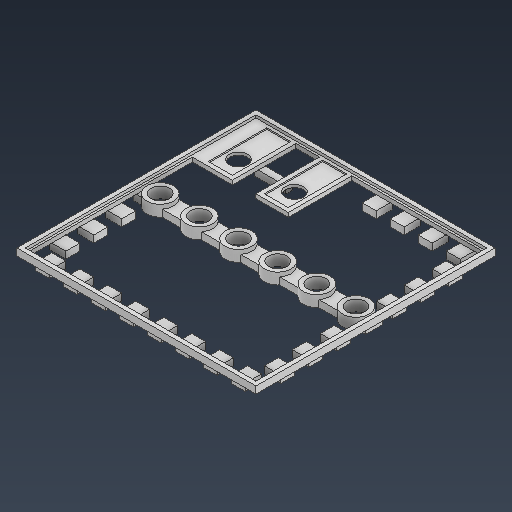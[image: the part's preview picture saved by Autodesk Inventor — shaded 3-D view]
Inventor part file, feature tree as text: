
AUTODESK INVENTOR PART (.ipt)
format: ipt  version: 2025.3 (Build 293356000, 356)  size: 868,864 bytes
history: native  units: mm
features: projected_geometry x26, sketch x20, extrude x8, fillet x1
ambient origin geometry x8: Origin, YZ Plane, XZ Plane, XY Plane, X Axis, Y Axis, Z Axis, Center Point
bodies: Solid1 (feature_tree)
feature tree (55):
  extrude  "Extrusion1"  Depth=171.0mm
  extrude  "Extrusion3"  Depth=60.0mm
  extrude  "Extrusion5"  Depth=78.0mm
  extrude  "Extrusion6"  Depth=75.0mm
  extrude  "Extrusion7"  Depth=30.0mm
  extrude  "Extrusion8"  Depth=5.0mm
  extrude  "Extrusion9"  Depth=5.0mm
  fillet  "Fillet1"  Radius=25.0mm
  extrude  "Extrusion10"  Depth=15.4mm
  sketch  "Sketch1"  dims[d0=171.0mm d1=171.0mm]
  sketch  "Sketch3"  dims[d10=78.0mm d11=78.0mm]
  sketch  "Sketch Rectangular Pattern1"  dims[d2=3.0mm d3=0.0mm d9=60.0mm]
  sketch  "Sketch Rectangular Pattern4"  dims[d12=60.0mm d17=75.0mm]
  sketch  "Sketch5"  dims[d20=5.0mm d21=30.0mm]
  sketch  "Sketch7"  dims[d32=15.4mm d33=15.4mm]
  projected_geometry  "Projected Loop3"
  sketch  "Sketch Rectangular Pattern5"  dims[d22=5.0mm d23=5.0mm]
  sketch  "Sketch8"  dims[d43=12.6mm]
  projected_geometry  "Projected Loop4"
  sketch  "Sketch Rectangular Pattern6"  dims[d27=5.0mm d28=5.0mm d31=25.0mm]
  sketch  "Sketch Rectangular Pattern7"  dims[d35=20.0mm d37=28.0mm d38=30.0mm d40=25.0mm]
  sketch  "Sketch Rectangular Pattern9"  dims[d44=6.3mm]
  sketch  "Sketch9"  dims[d45=4.0mm]
  projected_geometry  "Projected Loop5"
  projected_geometry  "Projected Loop6"
  projected_geometry  "Projected Loop7"
  projected_geometry  "Projected Loop8"
  projected_geometry  "Projected Loop9"
  projected_geometry  "Projected Loop10"
  projected_geometry  "Projected Loop11"
  projected_geometry  "Projected Loop12"
  sketch  "Sketch Rectangular Pattern11"  dims[d47=11.7mm]
  sketch  "Sketch Rectangular Pattern15"  dims[d52=15.4mm d53=15.4mm d54=28.0mm d55=25.0mm]
  projected_geometry  "Projected Loop26"
  projected_geometry  "Projected Loop27"
  projected_geometry  "Projected Loop28"
  projected_geometry  "Projected Loop29"
  projected_geometry  "Projected Loop30"
  projected_geometry  "Projected Loop31"
  projected_geometry  "Projected Loop32"
  projected_geometry  "Projected Loop33"
  projected_geometry  "Projected Loop34"
  projected_geometry  "Projected Loop35"
  projected_geometry  "Projected Loop36"
  projected_geometry  "Projected Loop37"
  projected_geometry  "Projected Loop38"
  projected_geometry  "Projected Loop39"
  projected_geometry  "Projected Loop40"
  projected_geometry  "Projected Loop41"
  sketch  "Sketch Rectangular Pattern16"  dims[d56=12.6mm]
  sketch  "Sketch Rectangular Pattern17"  dims[d57=30.0mm]
  sketch  "Sketch Rectangular Pattern18"  dims[d58=80.0mm]
  sketch  "Sketch Rectangular Pattern19"  dims[d59=25.0mm d60=25.0mm d61=20.0mm d62=40.0mm d63=8.0mm d64=8.0mm d65=10.0mm d66=0.0mm d67=80.0mm d68=16.2mm d69=16.2mm d70=16.2mm d71=28.0mm d72=28.0mm d73=12.0mm d74=12.8mm d75=12.8mm d76=12.8mm d77=13.0mm d78=60.0mm d80=28.0mm d81=10.0mm d83=10.0mm d85=11.5mm d86=163.0mm d87=65.0mm d88=95.0mm d89=88.0mm d90=13.0mm d91=13.0mm d92=30.0mm d93=40.0mm d94=17.5mm d99=13.0mm d100=28.8mm d101=17.2mm d102=17.2mm d103=1.0mm d104=0.0mm d105=4.0mm d106=4.0mm d107=4.0mm d108=4.0mm d109=4.0mm d110=4.0mm d111=7.0mm d112=4.0mm d113=4.0mm d114=4.0mm d115=4.5mm d116=5.0mm d117=22.0mm d118=12.0mm d119=6.0mm d120=10.0mm d121=0.0mm d122=3.0mm d123=60.0mm d125=28.0mm d126=10.0mm d128=10.0mm d130=3.0mm d131=3.0mm d132=3.0mm d133=3.0mm d134=3.0mm d135=10.0mm d136=6.0mm d137=80.0mm d139=20.0mm d140=10.0mm d142=10.0mm d145=10.0mm d146=40.0mm d148=20.0mm d149=10.0mm d151=10.0mm d153=16.0mm d154=10.0mm d162=10.0mm d163=16.0mm d164=5.0mm d165=0.0mm d166=30.0mm d168=20.0mm d169=10.0mm d171=10.0mm d181=10.0mm d182=80.0mm d184=20.0mm d185=10.0mm d187=10.0mm d215=10.0mm d216=0.0mm d217=6.0mm d218=70.0mm d220=20.0mm d221=10.0mm d223=10.0mm d225=10.0mm d226=10.0mm d227=10.0mm d228=10.0mm d229=10.0mm d230=10.0mm d231=10.0mm d232=10.0mm d233=30.0mm d235=20.0mm d236=10.0mm d238=10.0mm d240=40.0mm d242=20.0mm d243=10.0mm d245=10.0mm d247=30.0mm d249=20.0mm d250=10.0mm d252=10.0mm d254=30.0mm d256=20.0mm d257=10.0mm d259=10.0mm d261=2.7mm d262=10.0mm d263=0.0mm d264=1.0mm d265=3.0mm d266=2.0mm d267=0.0mm]
  sketch  "Sketch10"  dims[d46=14.0mm]
  sketch  "Sketch11"  dims[d49=20.0mm d51=30.0mm]
